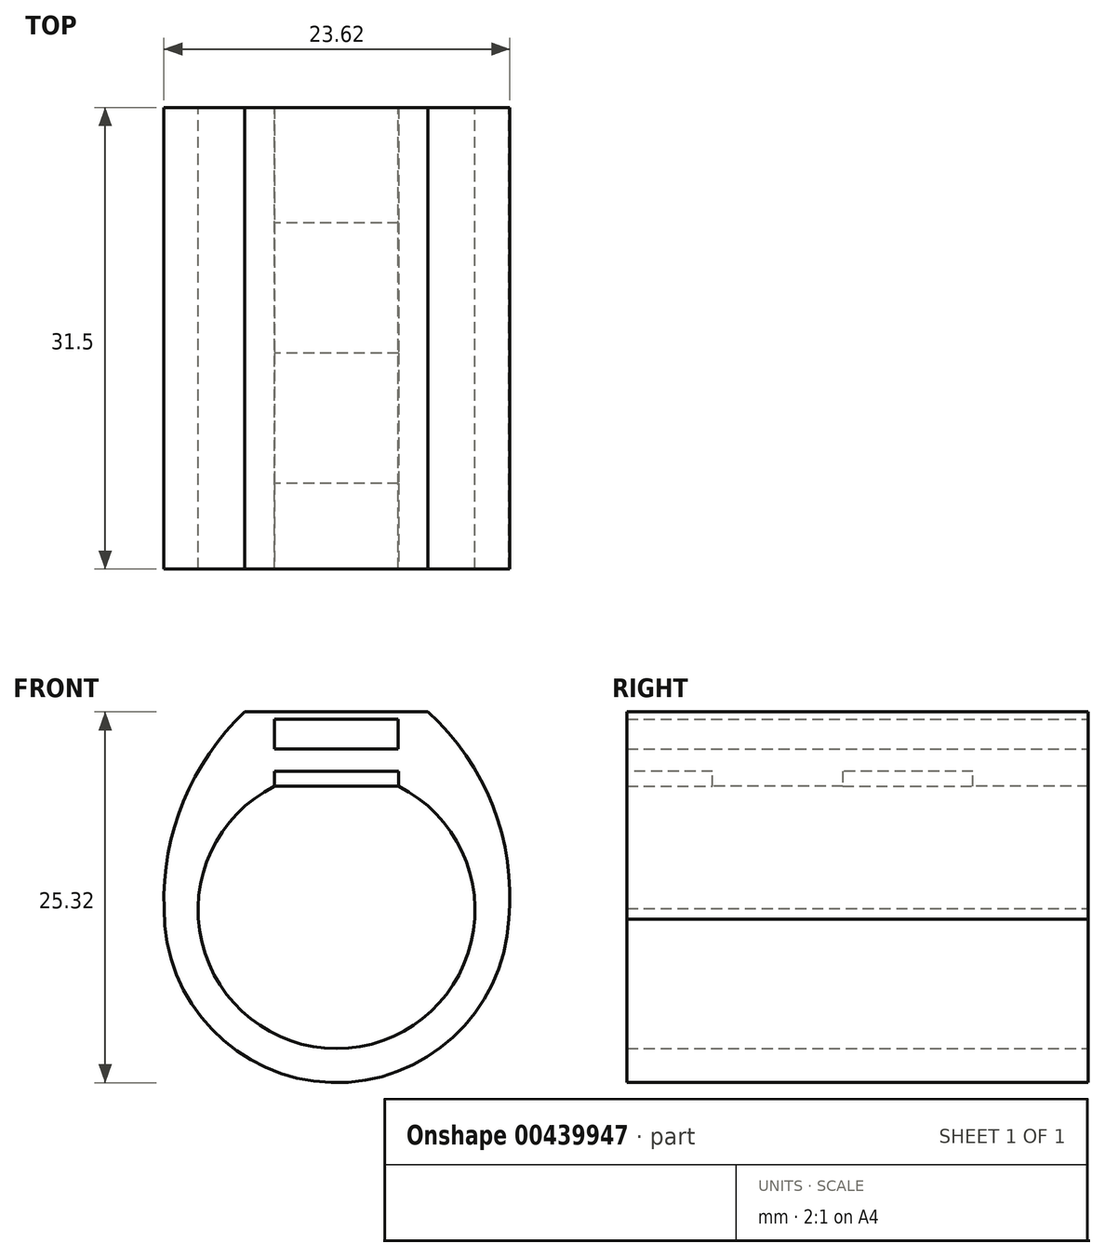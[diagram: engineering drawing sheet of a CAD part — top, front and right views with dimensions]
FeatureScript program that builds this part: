
annotation { "Feature Type Name" : "Feature", "Feature Type Description" : "" }
export const myFeature = defineFeature(function(context is Context, id is Id, definition is map)
    precondition{}
    {
        {
            var Q0;
            Q0=qCreatedBy(makeId("Right.planeOp"),FACE);
            var sketch = newSketch(context, id + "F0", { "sketchPlane" : qUnion([Q0])});
            skLineSegment(sketch, "E0", {"start": v(-15.75, 0) * mm, "end": v(15.75, 0) * mm});
            skLineSegment(sketch, "E1", {"start": v(15.75, 0) * mm, "end": v(15.75, -2.54) * mm});
            skLineSegment(sketch, "E2", {"start": v(15.75, -2.54) * mm, "end": v(7.87, -2.54) * mm});
            skLineSegment(sketch, "E3", {"start": v(7.87, -2.54) * mm, "end": v(7.87, -1.52) * mm});
            skLineSegment(sketch, "E4", {"start": v(7.87, -1.52) * mm, "end": v(-1.02, -1.52) * mm});
            skLineSegment(sketch, "E5", {"start": v(-1.02, -1.52) * mm, "end": v(-1.02, -2.54) * mm});
            skLineSegment(sketch, "E6", {"start": v(-1.02, -2.54) * mm, "end": v(-9.9, -2.54) * mm});
            skLineSegment(sketch, "E7", {"start": v(-9.9, -2.54) * mm, "end": v(-9.9, -1.52) * mm});
            skLineSegment(sketch, "E8", {"start": v(-9.9, -1.52) * mm, "end": v(-15.75, -1.52) * mm});
            skLineSegment(sketch, "E9", {"start": v(-15.75, -1.52) * mm, "end": v(-15.75, 0) * mm});
            skSolve(sketch);
        }
        {
            var Q0;
            Q0=makeQuery(id+"F0.imprint","IMPRINT",FACE,{"disambiguationData":[TD([[makeQuery(id+"F0.imprint","IMPRINT",EDGE,{"derivedFrom":sQuery(id+"F0.wireOp",EDGE,"E0")}),-1.0]])]});
            extrude(context, id + "F1", {"entities" : qUnion([Q0]), "endBound" : BoundingType.SYMMETRIC, "depth" : 8.46 * mm});
        }
        {
            var Q0;
            Q0=qCreatedBy(makeId("Front.planeOp"),FACE);
            var sketch = newSketch(context, id + "F2", { "sketchPlane" : qUnion([Q0])});
            skArc(sketch, "E10", {"start": v(-4.23, 0) * mm, "mid": v(0, -22.78) * mm, "end": v(4.23, 0) * mm});
            skArc(sketch, "E11", {"start": v(-4.23, -2.54) * mm, "mid": v(0, -20.45) * mm, "end": v(4.23, -2.54) * mm});
            skLineSegment(sketch, "E12", {"start": v(-4.23, 0) * mm, "end": v(-4.23, -2.54) * mm});
            skLineSegment(sketch, "E13", {"start": v(4.23, -2.54) * mm, "end": v(4.23, 0) * mm});
            skSolve(sketch);
        }
        {
            var Q0;
            Q0=qSketchRegion(id+"F2",true);
            extrude(context, id + "F3", {"entities" : qUnion([Q0]), "operationType" : NewBodyOperationType.ADD, "endBound" : BoundingType.SYMMETRIC, "depth" : 31.5 * mm});
        }
        {
            var Q0;
            Q0=qCreatedBy(makeId("Front.planeOp"),FACE);
            var sketch = newSketch(context, id + "F4", { "sketchPlane" : qUnion([Q0])});
            skLineSegment(sketch, "E14", {"start": v(6.25, 0) * mm, "end": v(6.25, 2.54) * mm});
            skLineSegment(sketch, "E15", {"start": v(-6.27, 2.54) * mm, "end": v(-6.26, 0) * mm});
            skLineSegment(sketch, "E16", {"start": v(-6.26, 0) * mm, "end": v(-4.23, 0) * mm});
            skLineSegment(sketch, "E17", {"start": v(6.25, 0) * mm, "end": v(4.22, 0) * mm});
            skLineSegment(sketch, "E18", {"start": v(-4.23, 0) * mm, "end": v(-4.23, 2.02) * mm});
            skLineSegment(sketch, "E19", {"start": v(4.22, 0) * mm, "end": v(4.22, 2.02) * mm});
            skLineSegment(sketch, "E20", {"start": v(-4.23, 2.02) * mm, "end": v(4.22, 2.02) * mm});
            skLineSegment(sketch, "E21", {"start": v(-6.27, 2.54) * mm, "end": v(6.25, 2.54) * mm});
            skSolve(sketch);
        }
        {
            var Q0;
            Q0=qSketchRegion(id+"F4",true);
            extrude(context, id + "F5", {"entities" : qUnion([Q0]), "operationType" : NewBodyOperationType.ADD, "endBound" : BoundingType.SYMMETRIC, "depth" : 31.5 * mm});
        }
        {
            var Q0;
            Q0=qCreatedBy(makeId("Front.planeOp"),FACE);
            var sketch = newSketch(context, id + "F6", { "sketchPlane" : qUnion([Q0])});
            skArc(sketch, "E22", {"start": v(11.56, -13.13) * mm, "mid": v(8.46, -6.25) * mm, "end": v(4.23, 0) * mm});
            skLineSegment(sketch, "E23", {"start": v(-6.27, 2.54) * mm, "end": v(-4.23, 0) * mm});
            skLineSegment(sketch, "E24", {"start": v(6.25, 2.54) * mm, "end": v(4.23, 0) * mm});
            skLineSegment(sketch, "E25", {"start": v(-13.96, -13.13) * mm, "end": v(14.66, -13.13) * mm, "construction": true});
            skArc(sketch, "E26", {"start": v(-6.27, 2.54) * mm, "mid": v(-10.85, -4.64) * mm, "end": v(-11.57, -13.13) * mm});
            skArc(sketch, "E27", {"start": v(11.56, -13.13) * mm, "mid": v(10.93, -4.6) * mm, "end": v(6.25, 2.54) * mm});
            skArc(sketch, "E28", {"start": v(-4.23, 0) * mm, "mid": v(-9, -5.95) * mm, "end": v(-11.57, -13.13) * mm});
            skSolve(sketch);
        }
        {
            var Q0;
            Q0=qSketchRegion(id+"F6",true);
            extrude(context, id + "F7", {"entities" : qUnion([Q0]), "operationType" : NewBodyOperationType.ADD, "endBound" : BoundingType.SYMMETRIC, "depth" : 31.5 * mm});
        }
    });
